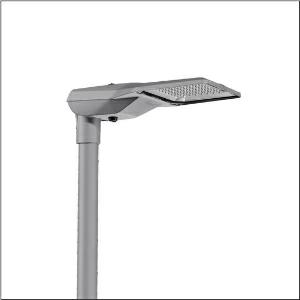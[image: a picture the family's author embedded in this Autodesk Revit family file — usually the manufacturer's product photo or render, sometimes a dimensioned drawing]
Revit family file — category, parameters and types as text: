
# Revit family: streetlight_sl_21_midi___st1_5a_5xe3p33t08mb_b96f
name_source: partatom
category: Lighting Fixtures
units: mm (PartAtom-declared; Revit-internal decimal feet)

## family parameters
Cut with Voids When Loaded = No
Host = Face
Light Source = No
Part Type = Normal
Room Calculation Point = No
Round Connector Dimension = Use Diameter
Shared = No

## types (1)
- --- (1 x LED, 17960 lm, 136 W, 3000K)
    Apparent Load = 136 VA
    CIE Flux Codes = 22 53 95 100 100
    Color Rendering = 70
    Color Temperature = 3000K
    Default Elevation = 1800 mm
    Description = Streetlight SL 21 midi, mast luminaire, primary light control with lens, of PMMA, primary optical cover: cover, of toughened safety glass, transparent, light distribution: ST1.5a, light emission: direct distribution, primary light characteristic: asymmetric, installation type: side-entry, post-top, LED, High Power LED, rated luminous flux: 17.960lm, luminous efficacy: 132lm/W, light colour: 730, colour temperature: 3000K, control: overheat protection, constant luminous flux control, time-dependent luminous flux control, flexible luminous flux parameterisation, presetting dimming logarithmic, mains connection: 230..240V, AC, 50/60Hz, start of lifetime: 136W, end of service life: 142W, reduction: 61W, luminaire housing, of diecast aluminium, powder-coated, Siteco® metallic grey (DB 702S), corrosivity category C5 mid according to DIN EN ISO 12944, please order mast flange separately, inclination adjustable: 0°, 5°, 10°, 15°, sealing non-destructively replaceable, multi-level sealing system, length: 644mm, width: 335mm, height: 110mm, mast flange for spigot size: 42mm (side-entry): 5XC10008XM4, 60/48mm (side-entry/post-top): 5XC10108XM2, 76/60mm (side-entry/post-top): 5XC10108XM1, Smart Interface below and above, protection rating (complete): IP66, insulation class (complete): insulation class II (safety insulation), certification: CE, ENEC, ENEC+, VDE, impact resistance: IK09, permissible operating ambient temperature for outdoor applications: -40..+50°C, standard-compliant lighting for roads and squares, packaging unit: 1 piece

Light Distribution: ST1.5a
    Height = 111 mm
    Lamp = 1 x LED
    Lamp Light Flux = 17960 lm
    Lamp Power = 136 W
    Lamp count = 1
    Length = 644 mm
    Luminous efficacy = 132 lm/W
    Manufacturer = Siteco
    ModVariant = No
    Model = 5XE3P33T08MB
    Number of Poles = 1
    OnlyDefault = Yes
    Power Factor = 1
    Product Name = Streetlight SL 21 midi | ST1.5a
    Product group = mast luminaire | pylon top
    ProductGroupID = 6100
    Protection Class = Protection class II
    Protection Degree = IP 66
    RLX_Detail_Level = 1
    RLX_Emergency_Light_Flux = 0 lm
    RLX_Emergency_Type = 0
    RLX_Emergency_Type_DB = No
    RlxData = <blob elided: 94093 chars, md5=091c8431>
    Socket = socket
    Standby Power = 0 W
    System Light Flux = 17960 lm
    System Power = 136 W
    Type Comments = factory setting: luminous flux: 100 % | dim-lin: 254 | 695 mA
    Type Image = l_1004304.jpg
    URL = http://relux.com
    VarID = @adj_127109
    Voltage = 0 V
    Weight = 0.00 kg
    Width = 336 mm

## geometry (parser evidence)
native form markers: Blend x4, Sweep x13
no freeform markers — native parametric forms only
